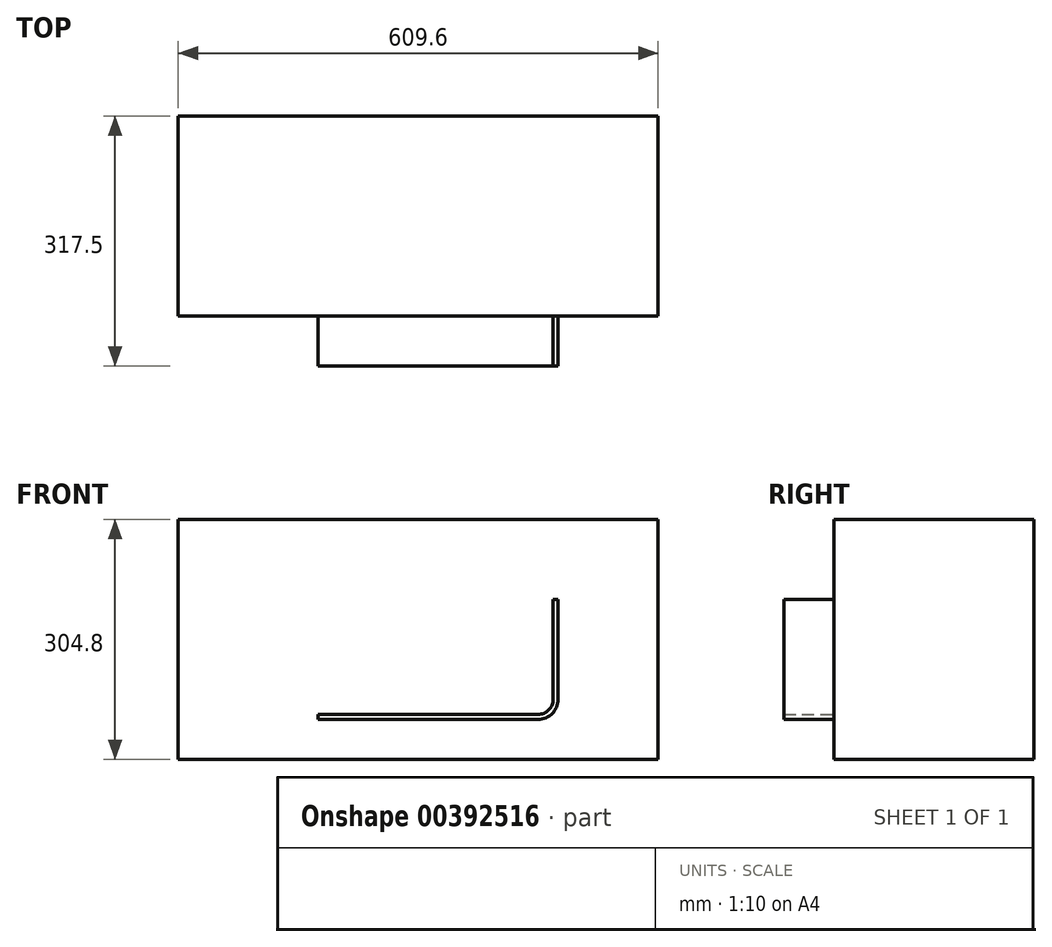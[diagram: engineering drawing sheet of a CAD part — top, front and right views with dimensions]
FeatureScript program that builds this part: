
annotation { "Feature Type Name" : "Feature", "Feature Type Description" : "" }
export const myFeature = defineFeature(function(context is Context, id is Id, definition is map)
    precondition{}
    {
        {
            var Q0;
            Q0=qCreatedBy(makeId("Front.planeOp"),FACE);
            var sketch = newSketch(context, id + "F0", { "sketchPlane" : qUnion([Q0])});
            skLineSegment(sketch, "E0.bottom", {"start": v(304.8, 152.4) * mm, "end": v(-304.8, 152.4) * mm});
            skLineSegment(sketch, "E0.top", {"start": v(304.8, -152.4) * mm, "end": v(-304.8, -152.4) * mm});
            skLineSegment(sketch, "E0.right", {"start": v(-304.8, 152.4) * mm, "end": v(-304.8, -152.4) * mm});
            skPoint(sketch, "E0.middle", {"position": v(0, 0) * mm});
            skLineSegment(sketch, "E1", {"start": v(304.8, 152.4) * mm, "end": v(304.8, -152.4) * mm});
            skSolve(sketch);
        }
        {
            var Q0;
            Q0=makeQuery(id+"F0.imprint","IMPRINT",FACE,{"disambiguationData":[TD([[makeQuery(id+"F0.imprint","IMPRINT",EDGE,{"derivedFrom":sQuery(id+"F0.wireOp",EDGE,"E0.bottom")}),1.0]])]});
            extrude(context, id + "F1", {"entities" : qUnion([Q0]), "endBound" : BoundingType.SYMMETRIC, "depth" : 254 * mm});
        }
        {
            var Q0;
            Q0=makeQuery(id+"F1.opExtrude","CAP_FACE",FACE,{"disambiguationData":[OSD([sQuery(id+"F0.wireOp",EDGE,"E0.bottom"),sQuery(id+"F0.wireOp",EDGE,"E0.top"),sQuery(id+"F0.wireOp",EDGE,"E0.right"),sQuery(id+"F0.wireOp",EDGE,"E1")])],"isStart":false});
            var sketch = newSketch(context, id + "F2", { "sketchPlane" : qUnion([Q0])});
            skLineSegment(sketch, "E2", {"start": v(177.8, 50.8) * mm, "end": v(177.8, -76.2) * mm});
            skLineSegment(sketch, "E3", {"start": v(152.4, -101.6) * mm, "end": v(-127, -101.6) * mm});
            skPoint(sketch, "E4.visualSharp", {"position": v(177.8, -101.6) * mm});
            skArc(sketch, "E4.filletArc", {"start": v(152.4, -101.6) * mm, "mid": v(170.36, -94.16) * mm, "end": v(177.8, -76.2) * mm});
            skLineSegment(sketch, "E5.0", {"start": v(152.4, -95.25) * mm, "end": v(-127, -95.25) * mm});
            skArc(sketch, "E5.1", {"start": v(152.4, -95.25) * mm, "mid": v(165.87, -89.67) * mm, "end": v(171.45, -76.2) * mm});
            skLineSegment(sketch, "E5.2", {"start": v(171.45, 50.8) * mm, "end": v(171.45, -76.2) * mm});
            skLineSegment(sketch, "E6", {"start": v(-127, -101.6) * mm, "end": v(-127, -95.25) * mm});
            skLineSegment(sketch, "E7", {"start": v(171.45, 50.8) * mm, "end": v(177.8, 50.8) * mm});
            skSolve(sketch);
        }
        {
            var Q0;
            Q0 = qSketchRegion(id + "F2", true);
            extrude(context, id + "F3", {"entities" : qUnion([Q0]), "depth" : 63.5 * mm});
        }
    });
